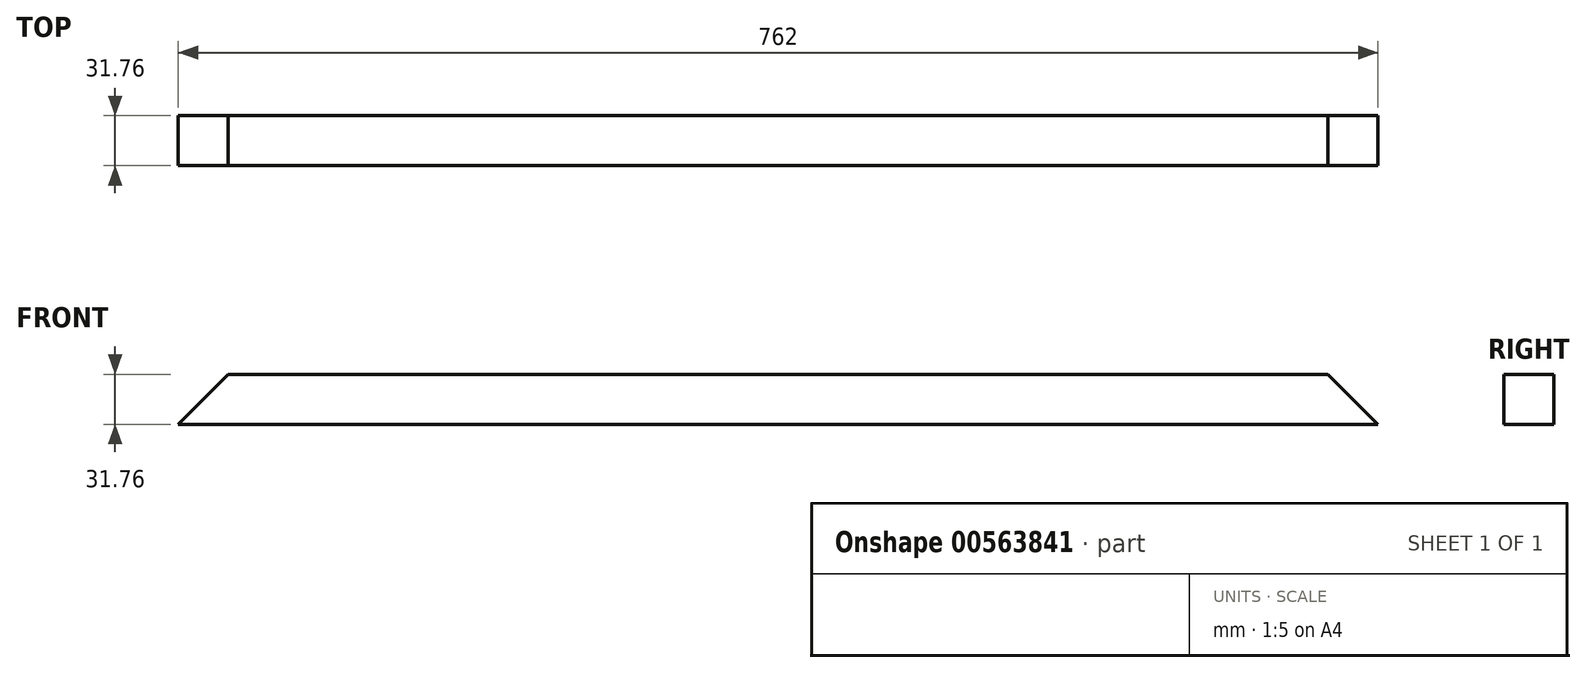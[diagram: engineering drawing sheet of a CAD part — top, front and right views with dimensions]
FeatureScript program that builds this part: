
annotation { "Feature Type Name" : "Feature", "Feature Type Description" : "" }
export const myFeature = defineFeature(function(context is Context, id is Id, definition is map)
    precondition{}
    {
        {
            var Q0;
            Q0=qCreatedBy(makeId("Front.planeOp"),FACE);
            var sketch = newSketch(context, id + "F0", { "sketchPlane" : qUnion([Q0])});
            skLineSegment(sketch, "E0.bottom", {"start": v(-381, 15.88) * mm, "end": v(381, 15.88) * mm});
            skLineSegment(sketch, "E0.top", {"start": v(-381, -15.87) * mm, "end": v(381, -15.87) * mm});
            skLineSegment(sketch, "E0.left", {"start": v(-381, 15.88) * mm, "end": v(-381, -15.87) * mm});
            skLineSegment(sketch, "E0.right", {"start": v(381, 15.88) * mm, "end": v(381, -15.87) * mm});
            skPoint(sketch, "E0.middle", {"position": v(0, 0) * mm});
            skLineSegment(sketch, "E1", {"start": v(-381, -15.88) * mm, "end": v(-349.25, 15.88) * mm});
            skLineSegment(sketch, "E2", {"start": v(381, -15.88) * mm, "end": v(349.25, 15.88) * mm});
            skSolve(sketch);
        }
        {
            var Q0;
            Q0=makeQuery(id+"F0.imprint","IMPRINT",FACE,{"disambiguationData":[TD([[makeQuery(id+"F0.imprint","IMPRINT",EDGE,{"derivedFrom":sQuery(id+"F0.wireOp",EDGE,"E0.top")}),1.0]])]});
            extrude(context, id + "F1", {"entities" : qUnion([Q0]), "endBound" : BoundingType.SYMMETRIC, "depth" : 31.75 * mm, "offsetDistance" : 25.4 * mm});
        }
    });
